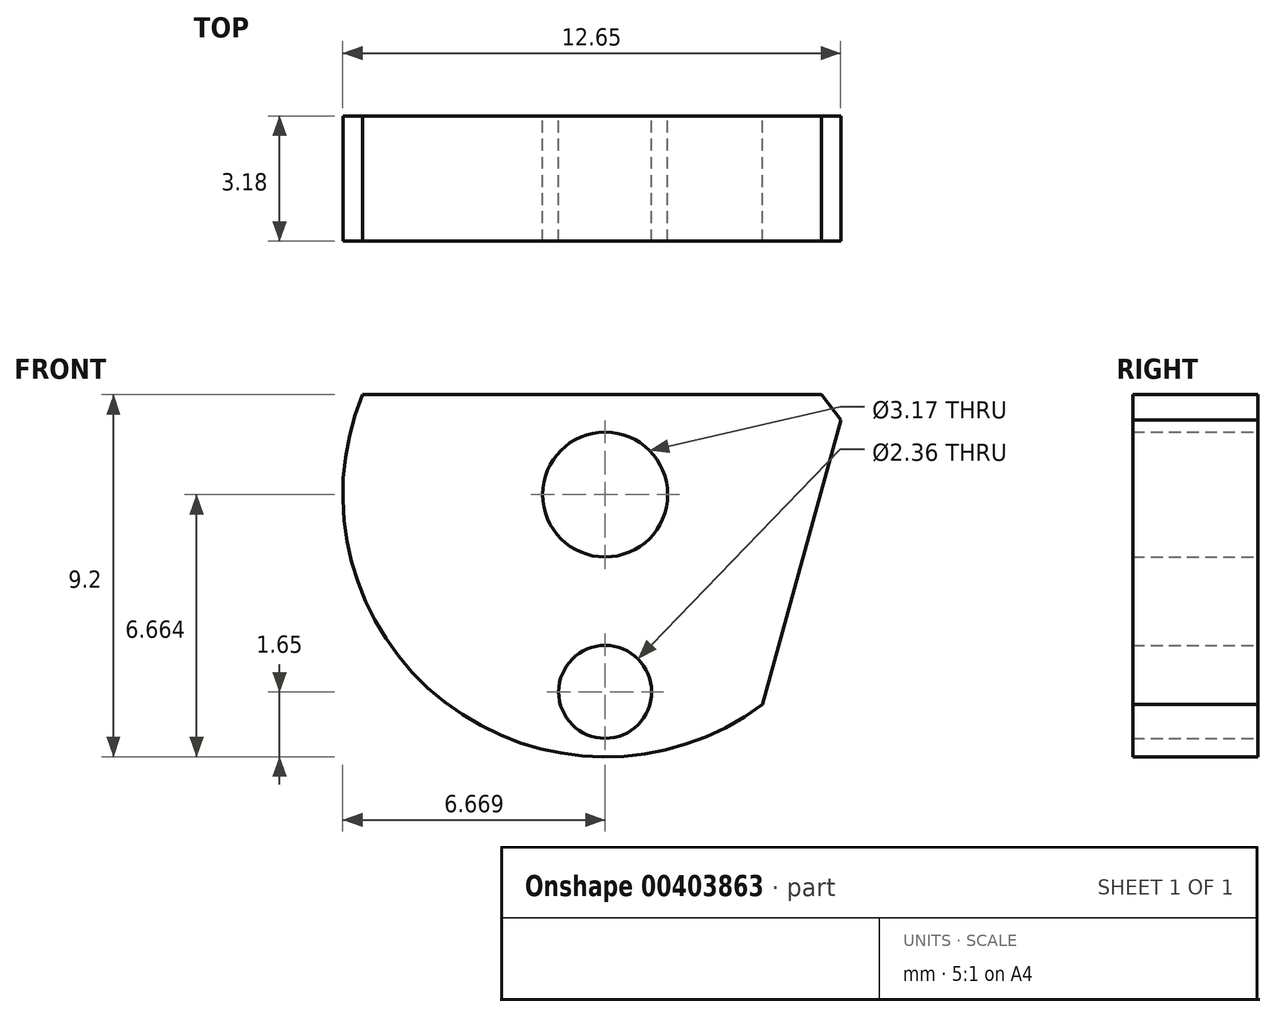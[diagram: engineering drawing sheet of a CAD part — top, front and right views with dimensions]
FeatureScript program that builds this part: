
annotation { "Feature Type Name" : "Feature", "Feature Type Description" : "" }
export const myFeature = defineFeature(function(context is Context, id is Id, definition is map)
    precondition{}
    {
        {
            var Q0;
            Q0=qCreatedBy(makeId("Front.planeOp"),FACE);
            var sketch = newSketch(context, id + "F0", { "sketchPlane" : qUnion([Q0])});
            skArc(sketch, "E0", {"start": v(-6.57, 4.1) * mm, "mid": v(-4.5, -3.71) * mm, "end": v(3.58, -3.78) * mm});
            skCircle(sketch, "E1", {"center": v(-0.41, 1.55) * mm, "radius": 1.59 * mm});
            skLineSegment(sketch, "E2", {"start": v(-6.57, 4.1) * mm, "end": v(5.75, 4.1) * mm});
            skCircle(sketch, "E3", {"center": v(-0.41, -3.46) * mm, "radius": 1.18 * mm});
            skLineSegment(sketch, "E4", {"start": v(5.75, 4.1) * mm, "end": v(3.58, -3.78) * mm});
            skSolve(sketch);
        }
        {
            var Q0;
            Q0=makeQuery(id+"F0.imprint","IMPRINT",FACE,{"disambiguationData":[TD([[makeQuery(id+"F0.imprint","IMPRINT",EDGE,{"derivedFrom":sQuery(id+"F0.wireOp",EDGE,"E0")}),1.0]])]});
            extrude(context, id + "F1", {"entities" : qUnion([Q0]), "endBound" : BoundingType.SYMMETRIC, "depth" : 3.17 * mm});
        }
        {
            var Q0;
            Q0=makeQuery(id+"F1.opExtrude","SWEPT_EDGE",EDGE,{"disambiguationData":[OSD([sQuery(id+"F0.wireOp",EDGE,"E2"),sQuery(id+"F0.wireOp",EDGE,"E4")])]});
            chamfer(context, id + "F2", {"entities" : qUnion([Q0]), "width" : 0.5 * mm, "tangentPropagation" : true});
        }
    });
